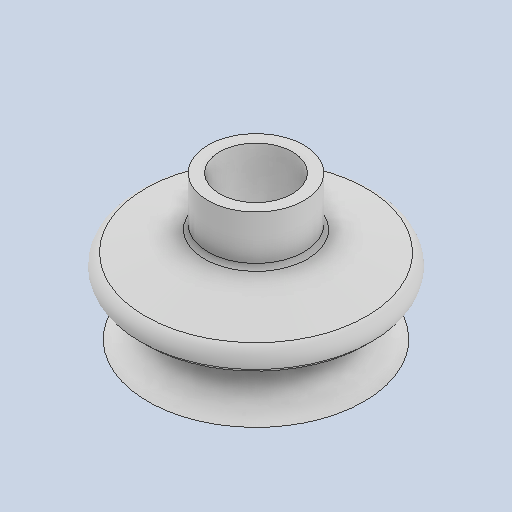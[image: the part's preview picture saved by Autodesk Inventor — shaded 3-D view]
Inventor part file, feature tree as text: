
AUTODESK INVENTOR PART (.ipt)
format: ipt  version: 2024 (Build 280153000, 153)  size: 201,216 bytes
history: native  units: mm
features: other x4, sketch x4
ambient origin geometry x8: Origin, YZ Plane, XZ Plane, XY Plane, X Axis, Y Axis, Z Axis, Center Point
bodies: Body1 (feature_tree)
feature tree (8):
  other  "VENTOSA_B.ipt"
  other  "Sólido1::VENTOSA_B.ipt"
  other  "OperaciónIdentificador1"
  sketch  "Boceto1"  dims[d0=10.0mm]
  sketch  "Boceto2"
  sketch  "Boceto3"
  sketch  "Boceto6"
  other  "Sólido1"
